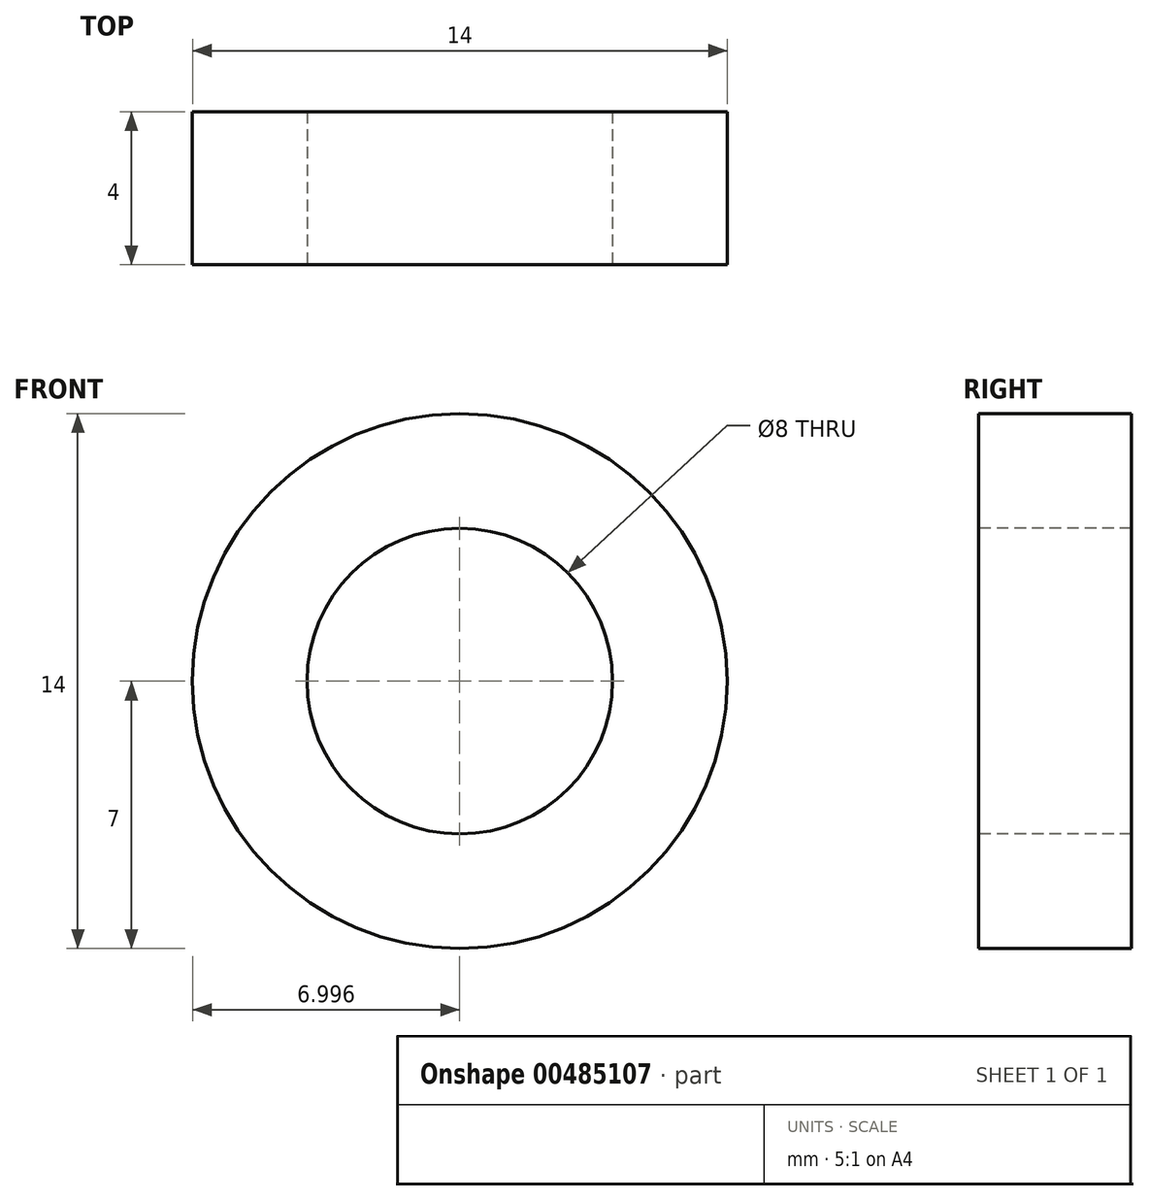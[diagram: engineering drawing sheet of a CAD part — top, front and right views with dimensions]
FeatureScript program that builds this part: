
annotation { "Feature Type Name" : "Feature", "Feature Type Description" : "" }
export const myFeature = defineFeature(function(context is Context, id is Id, definition is map)
    precondition{}
    {
        {
            var Q0;
            Q0=qCreatedBy(makeId("Front.planeOp"),FACE);
            var sketch = newSketch(context, id + "F0", { "sketchPlane" : qUnion([Q0])});
            skCircle(sketch, "E0", {"center": v(0.57, 0) * mm, "radius": 4 * mm});
            skCircle(sketch, "E1", {"center": v(0.57, 0) * mm, "radius": 7 * mm});
            skSolve(sketch);
        }
        {
            var Q0;
            Q0=makeQuery(id+"F0.imprint","IMPRINT",FACE,{"disambiguationData":[TD([[makeQuery(id+"F0.imprint","IMPRINT",EDGE,{"derivedFrom":sQuery(id+"F0.wireOp",EDGE,"E0")}),1.0]])]});
            extrude(context, id + "F1", {"entities" : qUnion([Q0]), "oppositeDirection" : true, "depth" : 4.5 * mm});
        }
        {
            var Q0;
            Q0=makeQuery(id+"F0.imprint","IMPRINT",FACE,{"disambiguationData":[TD([[makeQuery(id+"F0.imprint","IMPRINT",EDGE,{"derivedFrom":sQuery(id+"F0.wireOp",EDGE,"E0")}),-1.0]])]});
            extrude(context, id + "F2", {"entities" : qUnion([Q0]), "oppositeDirection" : true, "depth" : 4 * mm});
        }
        {
            var Q0;
            Q0=makeQuery(id+"F1.opExtrude","SWEPT_BODY",BODY,{"disambiguationData":[OSD([sQuery(id+"F0.wireOp",EDGE,"E0")])]});
            deleteBodies(context, id + "F3", {"entities" : qUnion([Q0])});
        }
    });
